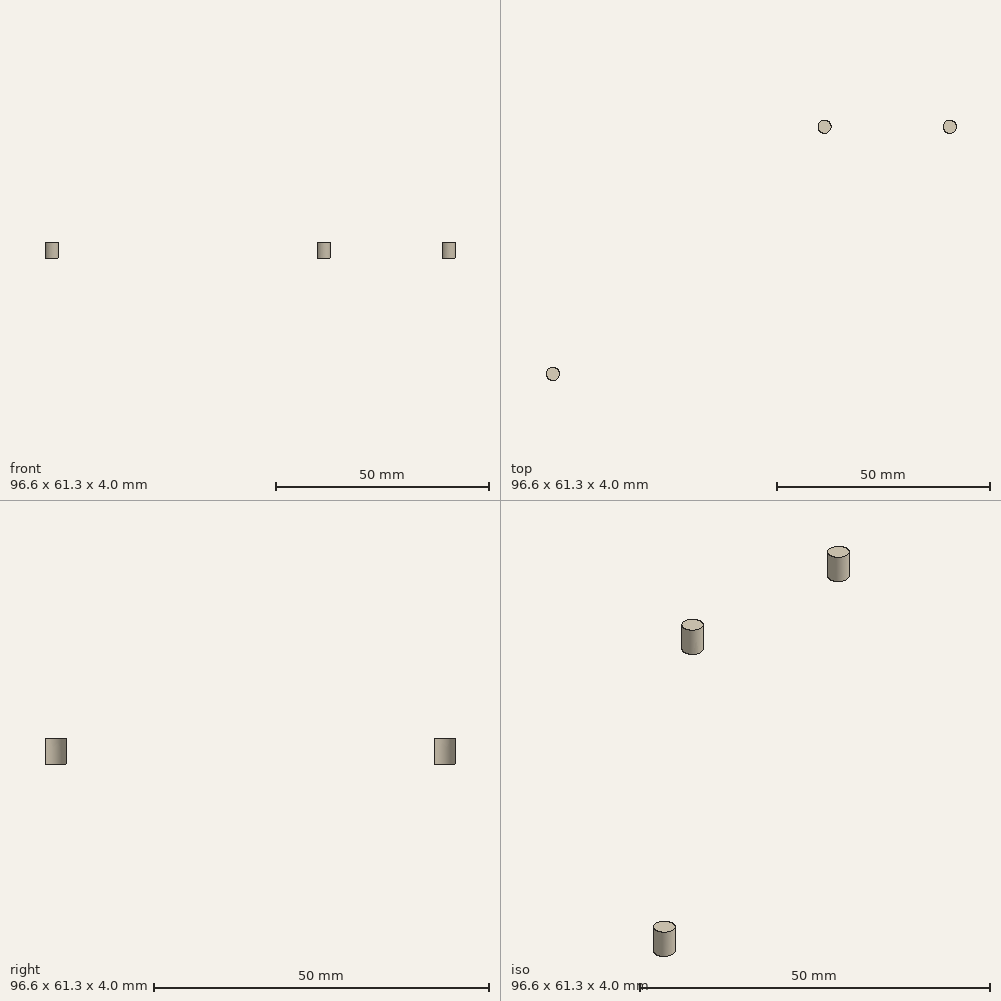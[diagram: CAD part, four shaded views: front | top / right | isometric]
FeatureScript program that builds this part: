
annotation { "Feature Type Name" : "Feature", "Feature Type Description" : "" }
export const myFeature = defineFeature(function(context is Context, id is Id, definition is map)
    precondition{}
    {
        {
            var Q0;
            Q0=qCreatedBy(makeId("Top.planeOp"),FACE);
            var sketch = newSketch(context, id + "F0", { "sketchPlane" : qUnion([Q0])});
            skLineSegment(sketch, "E0.bottom", {"start": v(0, 0) * mm, "end": v(-219, 0) * mm});
            skLineSegment(sketch, "E0.top", {"start": v(0, -219) * mm, "end": v(-219, -219) * mm});
            skLineSegment(sketch, "E0.left", {"start": v(0, 0) * mm, "end": v(0, -219) * mm});
            skLineSegment(sketch, "E0.right", {"start": v(-219, 0) * mm, "end": v(-219, -219) * mm});
            skLineSegment(sketch, "E1", {"start": v(-222.54, -3.54) * mm, "end": v(-219, 0) * mm});
            skLineSegment(sketch, "E2", {"start": v(-219, 0) * mm, "end": v(-215.46, 3.54) * mm});
            skLineSegment(sketch, "E3", {"start": v(-219, 0) * mm, "end": v(0, -219) * mm, "construction": true});
            skLineSegment(sketch, "E4.bottom", {"start": v(-222.54, -3.54) * mm, "end": v(-215.46, 3.54) * mm, "construction": true});
            skLineSegment(sketch, "E4.top", {"start": v(-3.54, -222.54) * mm, "end": v(3.54, -215.46) * mm, "construction": true});
            skLineSegment(sketch, "E4.left", {"start": v(-222.54, -3.54) * mm, "end": v(-3.54, -222.54) * mm, "construction": true});
            skLineSegment(sketch, "E4.right", {"start": v(-215.46, 3.54) * mm, "end": v(3.54, -215.46) * mm, "construction": true});
            skLineSegment(sketch, "E5.bottom", {"start": v(-3.54, 3.54) * mm, "end": v(3.54, -3.54) * mm, "construction": true});
            skLineSegment(sketch, "E5.top", {"start": v(-222.54, -215.46) * mm, "end": v(-215.46, -222.54) * mm, "construction": true});
            skLineSegment(sketch, "E5.left", {"start": v(-3.54, 3.54) * mm, "end": v(-222.54, -215.46) * mm, "construction": true});
            skLineSegment(sketch, "E5.right", {"start": v(3.54, -3.54) * mm, "end": v(-215.46, -222.54) * mm, "construction": true});
            skPoint(sketch, "E6", {"position": v(-215.46, -214.61) * mm});
            skPoint(sketch, "E7", {"position": v(-211.93, -219) * mm});
            skPoint(sketch, "E8", {"position": v(-109.5, -116.57) * mm});
            skPoint(sketch, "E9", {"position": v(-7.07, -219) * mm});
            skLineSegment(sketch, "E10", {"start": v(-211.93, -219) * mm, "end": v(-183.64, -190.72) * mm});
            skLineSegment(sketch, "E11", {"start": v(-183.64, -190.72) * mm, "end": v(-35.36, -190.72) * mm});
            skLineSegment(sketch, "E12", {"start": v(-35.36, -190.72) * mm, "end": v(-7.07, -219) * mm});
            skLineSegment(sketch, "E13", {"start": v(-211.93, -219) * mm, "end": v(-7.07, -219) * mm});
            skPoint(sketch, "E14", {"position": v(-219, -109.5) * mm});
            skPoint(sketch, "E15", {"position": v(0, -109.5) * mm});
            skLineSegment(sketch, "E16", {"start": v(-219, -109.5) * mm, "end": v(0, -109.5) * mm, "construction": true});
            skLineSegment(sketch, "E17.MirrorCS", {"start": v(-211.93, 0) * mm, "end": v(-7.07, 0) * mm});
            skLineSegment(sketch, "E18", {"start": v(-35.36, -28.28) * mm, "end": v(-7.07, 0) * mm});
            skLineSegment(sketch, "E19", {"start": v(-183.64, -28.28) * mm, "end": v(-211.93, 0) * mm});
            skLineSegment(sketch, "E20", {"start": v(-173.04, -180.1) * mm, "end": v(-45.96, -180.1) * mm});
            skLineSegment(sketch, "E21", {"start": v(-45.96, -180.1) * mm, "end": v(-35.36, -190.72) * mm});
            skLineSegment(sketch, "E22", {"start": v(-183.64, -190.72) * mm, "end": v(-173.04, -180.1) * mm});
            skLineSegment(sketch, "E23", {"start": v(-173.04, -180.1) * mm, "end": v(-109.5, -116.57) * mm});
            skLineSegment(sketch, "E24", {"start": v(-45.96, -180.1) * mm, "end": v(-109.5, -116.57) * mm});
            skLineSegment(sketch, "E25", {"start": v(-136.77, -143.84) * mm, "end": v(-82.23, -143.84) * mm});
            skLineSegment(sketch, "E26.MirrorCS", {"start": v(-222.54, -215.46) * mm, "end": v(-219, -219) * mm});
            skLineSegment(sketch, "E27.MirrorCS", {"start": v(-219, -219) * mm, "end": v(-215.46, -222.54) * mm});
            skLineSegment(sketch, "E28.MirrorCS", {"start": v(-183.64, -28.28) * mm, "end": v(-173.04, -38.9) * mm});
            skLineSegment(sketch, "E29.MirrorCS", {"start": v(-45.96, -38.9) * mm, "end": v(-35.36, -28.28) * mm});
            skLineSegment(sketch, "E30.MirrorCS", {"start": v(-45.96, -38.9) * mm, "end": v(-109.5, -102.43) * mm});
            skLineSegment(sketch, "E31.MirrorCS", {"start": v(-183.64, -190.72) * mm, "end": v(-211.93, -219) * mm});
            skLineSegment(sketch, "E32.MirrorCS", {"start": v(3.54, -215.46) * mm, "end": v(-215.46, 3.54) * mm, "construction": true});
            skLineSegment(sketch, "E33.MirrorCS", {"start": v(-183.64, -28.28) * mm, "end": v(-35.36, -28.28) * mm});
            skLineSegment(sketch, "E34.MirrorCS", {"start": v(-136.77, -75.16) * mm, "end": v(-82.23, -75.16) * mm});
            skLineSegment(sketch, "E35.MirrorCS", {"start": v(-219, -219) * mm, "end": v(0, 0) * mm, "construction": true});
            skPoint(sketch, "E36.MirrorP", {"position": v(-211.93, 0) * mm});
            skPoint(sketch, "E37.MirrorP", {"position": v(-7.07, 0) * mm});
            skLineSegment(sketch, "E38.MirrorCS", {"start": v(-173.04, -38.9) * mm, "end": v(-109.5, -102.43) * mm});
            skPoint(sketch, "E39.MirrorP", {"position": v(-109.5, -102.43) * mm});
            skPoint(sketch, "E40.MirrorP", {"position": v(-215.46, -4.39) * mm});
            skLineSegment(sketch, "E41.MirrorCS", {"start": v(-219, -219) * mm, "end": v(-219, 0) * mm});
            skLineSegment(sketch, "E42.MirrorCS", {"start": v(-3.54, -222.54) * mm, "end": v(-222.54, -3.54) * mm, "construction": true});
            skLineSegment(sketch, "E43.MirrorCS", {"start": v(-211.93, 0) * mm, "end": v(-183.64, -28.28) * mm});
            skLineSegment(sketch, "E44.MirrorCS", {"start": v(-222.54, -215.46) * mm, "end": v(-3.54, 3.54) * mm, "construction": true});
            skLineSegment(sketch, "E45.MirrorCS", {"start": v(-215.46, -222.54) * mm, "end": v(3.54, -3.54) * mm, "construction": true});
            skLineSegment(sketch, "E46.MirrorCS", {"start": v(-173.04, -38.9) * mm, "end": v(-45.96, -38.9) * mm});
            skLineSegment(sketch, "E47.MirrorCS", {"start": v(0, -219) * mm, "end": v(0, 0) * mm});
            skLineSegment(sketch, "E48", {"start": v(-219, -7.07) * mm, "end": v(-194.25, -31.82) * mm});
            skLineSegment(sketch, "E49", {"start": v(-190.72, -183.64) * mm, "end": v(-219, -211.93) * mm});
            skLineSegment(sketch, "E50", {"start": v(-219, -211.93) * mm, "end": v(-219, -7.07) * mm});
            skLineSegment(sketch, "E51", {"start": v(-194.25, -31.82) * mm, "end": v(-194.25, -71.82) * mm});
            skLineSegment(sketch, "E52", {"start": v(-194.25, -71.82) * mm, "end": v(-219, -96.57) * mm});
            skLineSegment(sketch, "E53.MirrorCS", {"start": v(-194.25, -147.18) * mm, "end": v(-219, -122.43) * mm});
            skLineSegment(sketch, "E54.MirrorCS", {"start": v(-194.25, -187.18) * mm, "end": v(-194.25, -147.18) * mm});
            skLineSegment(sketch, "E55", {"start": v(-194.25, -187.18) * mm, "end": v(-219, -211.93) * mm});
            skLineSegment(sketch, "E56", {"start": v(-219, -122.43) * mm, "end": v(-219, -211.93) * mm});
            skLineSegment(sketch, "E57", {"start": v(-219, -96.57) * mm, "end": v(-219, -7.07) * mm});
            skLineSegment(sketch, "E58", {"start": v(-109.5, -219) * mm, "end": v(-109.5, 0) * mm, "construction": true});
            skLineSegment(sketch, "E59", {"start": v(0, -96.57) * mm, "end": v(0, -122.43) * mm, "construction": true});
            skPoint(sketch, "E60", {"position": v(-24.75, -109.5) * mm});
            skLineSegment(sketch, "E61", {"start": v(0, -65) * mm, "end": v(0, -147.18) * mm});
            skLineSegment(sketch, "E62", {"start": v(0, -7.07) * mm, "end": v(-17.68, -24.75) * mm});
            skLineSegment(sketch, "E63", {"start": v(0, -65) * mm, "end": v(-17.68, -47.32) * mm});
            skLineSegment(sketch, "E64", {"start": v(-17.68, -47.32) * mm, "end": v(-17.68, -24.75) * mm});
            skLineSegment(sketch, "E65.MirrorCS", {"start": v(0, -154) * mm, "end": v(-17.68, -171.68) * mm});
            skLineSegment(sketch, "E66.MirrorCS", {"start": v(-17.68, -171.68) * mm, "end": v(-17.68, -194.25) * mm});
            skLineSegment(sketch, "E67", {"start": v(-17.68, -194.25) * mm, "end": v(0, -211.93) * mm});
            skLineSegment(sketch, "E68", {"start": v(0, -211.93) * mm, "end": v(0, -154) * mm});
            skPoint(sketch, "E69", {"position": v(0, -142) * mm});
            skPoint(sketch, "E70", {"position": v(0, -77) * mm});
            skLineSegment(sketch, "E71", {"start": v(-17.68, -122.43) * mm, "end": v(-17.68, -96.57) * mm});
            skLineSegment(sketch, "E72", {"start": v(-17.68, -122.43) * mm, "end": v(0, -142) * mm});
            skLineSegment(sketch, "E73", {"start": v(-17.68, -96.57) * mm, "end": v(0, -77) * mm});
            skLineSegment(sketch, "E74", {"start": v(-17.68, -122.43) * mm, "end": v(0, -122.43) * mm, "construction": true});
            skLineSegment(sketch, "E75", {"start": v(0, -96.57) * mm, "end": v(-17.68, -96.57) * mm, "construction": true});
            skLineSegment(sketch, "E76", {"start": v(-214, -91.57) * mm, "end": v(-214, -127.43) * mm});
            skLineSegment(sketch, "E77", {"start": v(-10, -55) * mm, "end": v(-10, -88.07) * mm});
            skLineSegment(sketch, "E78.MirrorCS", {"start": v(-10, -164) * mm, "end": v(-10, -130.93) * mm});
            skLineSegment(sketch, "E79.bottom", {"start": v(-145.72, -81.22) * mm, "end": v(-117.43, -109.5) * mm});
            skLineSegment(sketch, "E79.top", {"start": v(-174, -109.5) * mm, "end": v(-145.72, -137.78) * mm});
            skLineSegment(sketch, "E79.left", {"start": v(-145.72, -81.22) * mm, "end": v(-174, -109.5) * mm});
            skLineSegment(sketch, "E79.right", {"start": v(-117.43, -109.5) * mm, "end": v(-145.72, -137.78) * mm});
            skLineSegment(sketch, "E80", {"start": v(-174, -109.5) * mm, "end": v(-219, -109.5) * mm, "construction": true});
            skLineSegment(sketch, "E81", {"start": v(-149.25, -84.75) * mm, "end": v(-142.18, -84.75) * mm});
            skLineSegment(sketch, "E82.MirrorCS", {"start": v(-149.25, -134.25) * mm, "end": v(-142.18, -134.25) * mm});
            skLineSegment(sketch, "E83", {"start": v(-170.46, -105.96) * mm, "end": v(-170.46, -113.04) * mm});
            skLineSegment(sketch, "E84", {"start": v(-145.72, -81.22) * mm, "end": v(-145.72, -137.78) * mm, "construction": true});
            skLineSegment(sketch, "E85.MirrorCS", {"start": v(-120.97, -105.96) * mm, "end": v(-120.97, -113.04) * mm});
            skLineSegment(sketch, "E86.MirrorCS", {"start": v(-73.28, -81.22) * mm, "end": v(-45, -109.5) * mm});
            skLineSegment(sketch, "E87.MirrorCS", {"start": v(-73.28, -81.22) * mm, "end": v(-101.57, -109.5) * mm});
            skLineSegment(sketch, "E88.MirrorCS", {"start": v(-101.57, -109.5) * mm, "end": v(-73.28, -137.78) * mm});
            skLineSegment(sketch, "E89.MirrorCS", {"start": v(-45, -109.5) * mm, "end": v(-73.28, -137.78) * mm});
            skLineSegment(sketch, "E90.MirrorCS", {"start": v(-48.54, -105.96) * mm, "end": v(-48.54, -113.04) * mm});
            skLineSegment(sketch, "E91.MirrorCS", {"start": v(-69.75, -84.75) * mm, "end": v(-76.82, -84.75) * mm});
            skLineSegment(sketch, "E92.MirrorCS", {"start": v(-98.03, -105.96) * mm, "end": v(-98.03, -113.04) * mm});
            skLineSegment(sketch, "E93.MirrorCS", {"start": v(-69.75, -134.25) * mm, "end": v(-76.82, -134.25) * mm});
            skPoint(sketch, "E94", {"position": v(-5, -5) * mm});
            skCircle(sketch, "E95", {"center": v(-5, -5) * mm, "radius": 1.52 * mm});
            skCircle(sketch, "E96.MirrorC", {"center": v(-214, -5) * mm, "radius": 1.52 * mm});
            skCircle(sketch, "E97.MirrorC", {"center": v(-214, -214) * mm, "radius": 1.52 * mm});
            skCircle(sketch, "E98.MirrorC", {"center": v(-5, -214) * mm, "radius": 1.52 * mm});
            skSolve(sketch);
        }
        {
            var Q0;
            {var subQ19=sQuery(id+"F0.wireOp",EDGE,"E28.MirrorCS");Q0=makeQuery(id+"F0.imprint","IMPRINT",FACE,{"disambiguationData":[TD([[makeQuery(id+"F0.imprint","IMPRINT",EDGE,{"derivedFrom":subQ19}),-1.0]])]});}
            var Q1;
            Q1=makeQuery(id+"F0.imprint","IMPRINT",FACE,{"disambiguationData":[TD([[makeQuery(id+"F0.imprint","IMPRINT",EDGE,{"derivedFrom":sQuery(id+"F0.wireOp",EDGE,"E21")}),-1.0]])]});
            var Q2;
            {var subQ3=sQuery(id+"F0.wireOp",EDGE,"E25");Q2=makeQuery(id+"F0.imprint","IMPRINT",FACE,{"disambiguationData":[TD([[makeQuery(id+"F0.imprint","IMPRINT",EDGE,{"derivedFrom":subQ3}),1.0]])]});}
            var Q3;
            {var subQ3=sQuery(id+"F0.wireOp",EDGE,"E34.MirrorCS");Q3=makeQuery(id+"F0.imprint","IMPRINT",FACE,{"disambiguationData":[TD([[makeQuery(id+"F0.imprint","IMPRINT",EDGE,{"derivedFrom":subQ3}),-1.0]])]});}
            var Q4;
            Q4=makeQuery(id+"F0.imprint","IMPRINT",FACE,{"disambiguationData":[TD([[makeQuery(id+"F0.imprint","IMPRINT",EDGE,{"derivedFrom":sQuery(id+"F0.wireOp",EDGE,"E28.MirrorCS")}),1.0]])]});
            var Q5;
            {var subQ3=sQuery(id+"F0.wireOp",EDGE,"E81");Q5=makeQuery(id+"F0.imprint","IMPRINT",FACE,{"disambiguationData":[TD([[makeQuery(id+"F0.imprint","IMPRINT",EDGE,{"derivedFrom":subQ3}),1.0]])]});}
            var Q6;
            {var subQ3=sQuery(id+"F0.wireOp",EDGE,"E83");Q6=makeQuery(id+"F0.imprint","IMPRINT",FACE,{"disambiguationData":[TD([[makeQuery(id+"F0.imprint","IMPRINT",EDGE,{"derivedFrom":subQ3}),-1.0]])]});}
            var Q7;
            {var subQ3=sQuery(id+"F0.wireOp",EDGE,"E82.MirrorCS");Q7=makeQuery(id+"F0.imprint","IMPRINT",FACE,{"disambiguationData":[TD([[makeQuery(id+"F0.imprint","IMPRINT",EDGE,{"derivedFrom":subQ3}),-1.0]])]});}
            var Q8;
            {var subQ3=sQuery(id+"F0.wireOp",EDGE,"E85.MirrorCS");Q8=makeQuery(id+"F0.imprint","IMPRINT",FACE,{"disambiguationData":[TD([[makeQuery(id+"F0.imprint","IMPRINT",EDGE,{"derivedFrom":subQ3}),1.0]])]});}
            var Q9;
            {var subQ3=sQuery(id+"F0.wireOp",EDGE,"E91.MirrorCS");Q9=makeQuery(id+"F0.imprint","IMPRINT",FACE,{"disambiguationData":[TD([[makeQuery(id+"F0.imprint","IMPRINT",EDGE,{"derivedFrom":subQ3}),-1.0]])]});}
            var Q10;
            {var subQ3=sQuery(id+"F0.wireOp",EDGE,"E92.MirrorCS");Q10=makeQuery(id+"F0.imprint","IMPRINT",FACE,{"disambiguationData":[TD([[makeQuery(id+"F0.imprint","IMPRINT",EDGE,{"derivedFrom":subQ3}),-1.0]])]});}
            var Q11;
            {var subQ3=sQuery(id+"F0.wireOp",EDGE,"E93.MirrorCS");Q11=makeQuery(id+"F0.imprint","IMPRINT",FACE,{"disambiguationData":[TD([[makeQuery(id+"F0.imprint","IMPRINT",EDGE,{"derivedFrom":subQ3}),1.0]])]});}
            var Q12;
            {var subQ3=sQuery(id+"F0.wireOp",EDGE,"E90.MirrorCS");Q12=makeQuery(id+"F0.imprint","IMPRINT",FACE,{"disambiguationData":[TD([[makeQuery(id+"F0.imprint","IMPRINT",EDGE,{"derivedFrom":subQ3}),1.0]])]});}
            extrude(context, id + "F1", {"entities" : qUnion([Q0, Q1, Q2, Q3, Q4, Q5, Q6, Q7, Q8, Q9, Q10, Q11, Q12]), "depth" : 4 * mm, "offsetDistance" : 25 * mm});
        }
        {
            var Q0;
            Q0=makeQuery(id+"F1.opExtrude","SWEPT_EDGE",EDGE,{"disambiguationData":[OSD([sQuery(id+"F0.wireOp",EDGE,"E79.left"),sQuery(id+"F0.wireOp",EDGE,"E81")])]});
            var Q1;
            Q1=makeQuery(id+"F1.opExtrude","SWEPT_EDGE",EDGE,{"disambiguationData":[OSD([sQuery(id+"F0.wireOp",EDGE,"E79.bottom"),sQuery(id+"F0.wireOp",EDGE,"E81")])]});
            var Q2;
            Q2=makeQuery(id+"F1.opExtrude","SWEPT_EDGE",EDGE,{"disambiguationData":[OSD([sQuery(id+"F0.wireOp",EDGE,"E79.left"),sQuery(id+"F0.wireOp",EDGE,"E83")])]});
            var Q3;
            Q3=makeQuery(id+"F1.opExtrude","SWEPT_EDGE",EDGE,{"disambiguationData":[OSD([sQuery(id+"F0.wireOp",EDGE,"E79.top"),sQuery(id+"F0.wireOp",EDGE,"E83")])]});
            var Q4;
            Q4=makeQuery(id+"F1.opExtrude","SWEPT_EDGE",EDGE,{"disambiguationData":[OSD([sQuery(id+"F0.wireOp",EDGE,"E79.right"),sQuery(id+"F0.wireOp",EDGE,"E85.MirrorCS")])]});
            var Q5;
            Q5=makeQuery(id+"F1.opExtrude","SWEPT_EDGE",EDGE,{"disambiguationData":[OSD([sQuery(id+"F0.wireOp",EDGE,"E79.bottom"),sQuery(id+"F0.wireOp",EDGE,"E85.MirrorCS")])]});
            var Q6;
            Q6=makeQuery(id+"F1.opExtrude","SWEPT_EDGE",EDGE,{"disambiguationData":[OSD([sQuery(id+"F0.wireOp",EDGE,"E79.right"),sQuery(id+"F0.wireOp",EDGE,"E82.MirrorCS")])]});
            var Q7;
            Q7=makeQuery(id+"F1.opExtrude","SWEPT_EDGE",EDGE,{"disambiguationData":[OSD([sQuery(id+"F0.wireOp",EDGE,"E79.top"),sQuery(id+"F0.wireOp",EDGE,"E82.MirrorCS")])]});
            var Q8;
            Q8=makeQuery(id+"F1.opExtrude","SWEPT_EDGE",EDGE,{"disambiguationData":[OSD([sQuery(id+"F0.wireOp",EDGE,"E87.MirrorCS"),sQuery(id+"F0.wireOp",EDGE,"E91.MirrorCS")])]});
            var Q9;
            Q9=makeQuery(id+"F1.opExtrude","SWEPT_EDGE",EDGE,{"disambiguationData":[OSD([sQuery(id+"F0.wireOp",EDGE,"E86.MirrorCS"),sQuery(id+"F0.wireOp",EDGE,"E91.MirrorCS")])]});
            var Q10;
            Q10=makeQuery(id+"F1.opExtrude","SWEPT_EDGE",EDGE,{"disambiguationData":[OSD([sQuery(id+"F0.wireOp",EDGE,"E87.MirrorCS"),sQuery(id+"F0.wireOp",EDGE,"E92.MirrorCS")])]});
            var Q11;
            Q11=makeQuery(id+"F1.opExtrude","SWEPT_EDGE",EDGE,{"disambiguationData":[OSD([sQuery(id+"F0.wireOp",EDGE,"E88.MirrorCS"),sQuery(id+"F0.wireOp",EDGE,"E92.MirrorCS")])]});
            var Q12;
            Q12=makeQuery(id+"F1.opExtrude","SWEPT_EDGE",EDGE,{"disambiguationData":[OSD([sQuery(id+"F0.wireOp",EDGE,"E86.MirrorCS"),sQuery(id+"F0.wireOp",EDGE,"E90.MirrorCS")])]});
            var Q13;
            Q13=makeQuery(id+"F1.opExtrude","SWEPT_EDGE",EDGE,{"disambiguationData":[OSD([sQuery(id+"F0.wireOp",EDGE,"E89.MirrorCS"),sQuery(id+"F0.wireOp",EDGE,"E90.MirrorCS")])]});
            var Q14;
            Q14=makeQuery(id+"F1.opExtrude","SWEPT_EDGE",EDGE,{"disambiguationData":[OSD([sQuery(id+"F0.wireOp",EDGE,"E89.MirrorCS"),sQuery(id+"F0.wireOp",EDGE,"E93.MirrorCS")])]});
            var Q15;
            Q15=makeQuery(id+"F1.opExtrude","SWEPT_EDGE",EDGE,{"disambiguationData":[OSD([sQuery(id+"F0.wireOp",EDGE,"E88.MirrorCS"),sQuery(id+"F0.wireOp",EDGE,"E93.MirrorCS")])]});
            var Q16;
            Q16=makeQuery(id+"F1.opExtrude","SWEPT_EDGE",EDGE,{"disambiguationData":[OSD([sQuery(id+"F0.wireOp",EDGE,"E23"),sQuery(id+"F0.wireOp",EDGE,"E25")])]});
            var Q17;
            Q17=makeQuery(id+"F1.opExtrude","SWEPT_EDGE",EDGE,{"disambiguationData":[OSD([sQuery(id+"F0.wireOp",EDGE,"E24"),sQuery(id+"F0.wireOp",EDGE,"E25")])]});
            var Q18;
            Q18=makeQuery(id+"F1.opExtrude","SWEPT_EDGE",EDGE,{"disambiguationData":[OSD([sQuery(id+"F0.wireOp",EDGE,"E30.MirrorCS"),sQuery(id+"F0.wireOp",EDGE,"E34.MirrorCS")])]});
            var Q19;
            Q19=makeQuery(id+"F1.opExtrude","SWEPT_EDGE",EDGE,{"disambiguationData":[OSD([sQuery(id+"F0.wireOp",EDGE,"E38.MirrorCS"),sQuery(id+"F0.wireOp",EDGE,"E34.MirrorCS")])]});
            var Q20;
            Q20=makeQuery(id+"F1.opExtrude","SWEPT_EDGE",EDGE,{"disambiguationData":[OSD([sQuery(id+"F0.wireOp",EDGE,"E21"),sQuery(id+"F0.wireOp",EDGE,"E12"),sQuery(id+"F0.wireOp",EDGE,"E11")])]});
            var Q21;
            Q21=makeQuery(id+"F1.opExtrude","SWEPT_EDGE",EDGE,{"disambiguationData":[OSD([sQuery(id+"F0.wireOp",EDGE,"E22"),sQuery(id+"F0.wireOp",EDGE,"E31.MirrorCS"),sQuery(id+"F0.wireOp",EDGE,"E11")])]});
            var Q22;
            Q22=makeQuery(id+"F1.opExtrude","SWEPT_EDGE",EDGE,{"disambiguationData":[OSD([sQuery(id+"F0.wireOp",EDGE,"E28.MirrorCS"),sQuery(id+"F0.wireOp",EDGE,"E19"),sQuery(id+"F0.wireOp",EDGE,"E33.MirrorCS")])]});
            var Q23;
            Q23=makeQuery(id+"F1.opExtrude","SWEPT_EDGE",EDGE,{"disambiguationData":[OSD([sQuery(id+"F0.wireOp",EDGE,"E29.MirrorCS"),sQuery(id+"F0.wireOp",EDGE,"E18"),sQuery(id+"F0.wireOp",EDGE,"E33.MirrorCS")])]});
            var Q24;
            Q24=makeQuery(id+"F1.opExtrude","SWEPT_EDGE",EDGE,{"disambiguationData":[OSD([sQuery(id+"F0.wireOp",EDGE,"E62"),sQuery(id+"F0.wireOp",EDGE,"E64")])]});
            var Q25;
            Q25=makeQuery(id+"F1.opExtrude","SWEPT_EDGE",EDGE,{"disambiguationData":[OSD([sQuery(id+"F0.wireOp",EDGE,"E63"),sQuery(id+"F0.wireOp",EDGE,"E64")])]});
            var Q26;
            Q26=makeQuery(id+"F1.opExtrude","SWEPT_EDGE",EDGE,{"disambiguationData":[OSD([sQuery(id+"F0.wireOp",EDGE,"E63"),sQuery(id+"F0.wireOp",EDGE,"E77")])]});
            var Q27;
            Q27=makeQuery(id+"F1.opExtrude","SWEPT_EDGE",EDGE,{"disambiguationData":[OSD([sQuery(id+"F0.wireOp",EDGE,"E73"),sQuery(id+"F0.wireOp",EDGE,"E77")])]});
            var Q28;
            Q28=makeQuery(id+"F1.opExtrude","SWEPT_EDGE",EDGE,{"disambiguationData":[OSD([sQuery(id+"F0.wireOp",EDGE,"E71"),sQuery(id+"F0.wireOp",EDGE,"E73")])]});
            var Q29;
            Q29=makeQuery(id+"F1.opExtrude","SWEPT_EDGE",EDGE,{"disambiguationData":[OSD([sQuery(id+"F0.wireOp",EDGE,"E71"),sQuery(id+"F0.wireOp",EDGE,"E72")])]});
            var Q30;
            Q30=makeQuery(id+"F1.opExtrude","SWEPT_EDGE",EDGE,{"disambiguationData":[OSD([sQuery(id+"F0.wireOp",EDGE,"E72"),sQuery(id+"F0.wireOp",EDGE,"E78.MirrorCS")])]});
            var Q31;
            Q31=makeQuery(id+"F1.opExtrude","SWEPT_EDGE",EDGE,{"disambiguationData":[OSD([sQuery(id+"F0.wireOp",EDGE,"E65.MirrorCS"),sQuery(id+"F0.wireOp",EDGE,"E78.MirrorCS")])]});
            var Q32;
            Q32=makeQuery(id+"F1.opExtrude","SWEPT_EDGE",EDGE,{"disambiguationData":[OSD([sQuery(id+"F0.wireOp",EDGE,"E65.MirrorCS"),sQuery(id+"F0.wireOp",EDGE,"E66.MirrorCS")])]});
            var Q33;
            Q33=makeQuery(id+"F1.opExtrude","SWEPT_EDGE",EDGE,{"disambiguationData":[OSD([sQuery(id+"F0.wireOp",EDGE,"E66.MirrorCS"),sQuery(id+"F0.wireOp",EDGE,"E67")])]});
            var Q34;
            Q34=makeQuery(id+"F1.opExtrude","SWEPT_EDGE",EDGE,{"disambiguationData":[OSD([sQuery(id+"F0.wireOp",EDGE,"E51"),sQuery(id+"F0.wireOp",EDGE,"E52")])]});
            var Q35;
            Q35=makeQuery(id+"F1.opExtrude","SWEPT_EDGE",EDGE,{"disambiguationData":[OSD([sQuery(id+"F0.wireOp",EDGE,"E48"),sQuery(id+"F0.wireOp",EDGE,"E51")])]});
            var Q36;
            Q36=makeQuery(id+"F1.opExtrude","SWEPT_EDGE",EDGE,{"disambiguationData":[OSD([sQuery(id+"F0.wireOp",EDGE,"E52"),sQuery(id+"F0.wireOp",EDGE,"E76")])]});
            var Q37;
            Q37=makeQuery(id+"F1.opExtrude","SWEPT_EDGE",EDGE,{"disambiguationData":[OSD([sQuery(id+"F0.wireOp",EDGE,"E53.MirrorCS"),sQuery(id+"F0.wireOp",EDGE,"E76")])]});
            var Q38;
            Q38=makeQuery(id+"F1.opExtrude","SWEPT_EDGE",EDGE,{"disambiguationData":[OSD([sQuery(id+"F0.wireOp",EDGE,"E53.MirrorCS"),sQuery(id+"F0.wireOp",EDGE,"E54.MirrorCS")])]});
            var Q39;
            Q39=makeQuery(id+"F1.opExtrude","SWEPT_EDGE",EDGE,{"disambiguationData":[OSD([sQuery(id+"F0.wireOp",EDGE,"E54.MirrorCS"),sQuery(id+"F0.wireOp",EDGE,"E55")])]});
            fillet(context, id + "F2", {"entities" : qUnion([Q0, Q1, Q2, Q3, Q4, Q5, Q6, Q7, Q8, Q9, Q10, Q11, Q12, Q13, Q14, Q15, Q16, Q17, Q18, Q19, Q20, Q21, Q22, Q23, Q24, Q25, Q26, Q27, Q28, Q29, Q30, Q31, Q32, Q33, Q34, Q35, Q36, Q37, Q38, Q39]), "radius" : 5 * mm, "tangentPropagation" : true, "allowEdgeOverflow" : false});
        }
        {
            var Q0;
            Q0=makeQuery(id+"F1.opExtrude","SWEPT_EDGE",EDGE,{"disambiguationData":[OSD([sQuery(id+"F0.wireOp",EDGE,"E21"),sQuery(id+"F0.wireOp",EDGE,"E24"),sQuery(id+"F0.wireOp",EDGE,"E20")])]});
            var Q1;
            Q1=makeQuery(id+"F1.opExtrude","SWEPT_EDGE",EDGE,{"disambiguationData":[OSD([sQuery(id+"F0.wireOp",EDGE,"E22"),sQuery(id+"F0.wireOp",EDGE,"E23"),sQuery(id+"F0.wireOp",EDGE,"E20")])]});
            var Q2;
            Q2=makeQuery(id+"F1.opExtrude","SWEPT_EDGE",EDGE,{"disambiguationData":[OSD([sQuery(id+"F0.wireOp",EDGE,"E28.MirrorCS"),sQuery(id+"F0.wireOp",EDGE,"E38.MirrorCS"),sQuery(id+"F0.wireOp",EDGE,"E46.MirrorCS")])]});
            var Q3;
            Q3=makeQuery(id+"F1.opExtrude","SWEPT_EDGE",EDGE,{"disambiguationData":[OSD([sQuery(id+"F0.wireOp",EDGE,"E29.MirrorCS"),sQuery(id+"F0.wireOp",EDGE,"E30.MirrorCS"),sQuery(id+"F0.wireOp",EDGE,"E46.MirrorCS")])]});
            fillet(context, id + "F3", {"entities" : qUnion([Q0, Q1, Q2, Q3]), "radius" : 3 * mm, "tangentPropagation" : true, "allowEdgeOverflow" : false});
        }
        {
            var Q0;
            Q0=makeQuery(id+"F1.opExtrude","SWEPT_EDGE",EDGE,{"disambiguationData":[OSD([sQuery(id+"F0.wireOp",EDGE,"E0.bottom"),sQuery(id+"F0.wireOp",EDGE,"E0.right")])]});
            var Q1;
            Q1=makeQuery(id+"F1.opExtrude","SWEPT_EDGE",EDGE,{"disambiguationData":[OSD([sQuery(id+"F0.wireOp",EDGE,"E0.right"),sQuery(id+"F0.wireOp",EDGE,"E48"),sQuery(id+"F0.wireOp",EDGE,"E57")])]});
            var Q2;
            Q2=makeQuery(id+"F1.opExtrude","SWEPT_EDGE",EDGE,{"disambiguationData":[OSD([sQuery(id+"F0.wireOp",EDGE,"E19"),sQuery(id+"F0.wireOp",EDGE,"E0.bottom"),sQuery(id+"F0.wireOp",EDGE,"E17.MirrorCS")])]});
            var Q3;
            Q3=makeQuery(id+"F1.opExtrude","SWEPT_EDGE",EDGE,{"disambiguationData":[OSD([sQuery(id+"F0.wireOp",EDGE,"E18"),sQuery(id+"F0.wireOp",EDGE,"E0.bottom"),sQuery(id+"F0.wireOp",EDGE,"E17.MirrorCS")])]});
            var Q4;
            Q4=makeQuery(id+"F1.opExtrude","SWEPT_EDGE",EDGE,{"disambiguationData":[OSD([sQuery(id+"F0.wireOp",EDGE,"E0.bottom"),sQuery(id+"F0.wireOp",EDGE,"E0.left")])]});
            var Q5;
            Q5=makeQuery(id+"F1.opExtrude","SWEPT_EDGE",EDGE,{"disambiguationData":[OSD([sQuery(id+"F0.wireOp",EDGE,"E0.left"),sQuery(id+"F0.wireOp",EDGE,"E62")])]});
            var Q6;
            Q6=makeQuery(id+"F1.opExtrude","SWEPT_EDGE",EDGE,{"disambiguationData":[OSD([sQuery(id+"F0.wireOp",EDGE,"E0.top"),sQuery(id+"F0.wireOp",EDGE,"E0.left")])]});
            var Q7;
            Q7=makeQuery(id+"F1.opExtrude","SWEPT_EDGE",EDGE,{"disambiguationData":[OSD([sQuery(id+"F0.wireOp",EDGE,"E0.top"),sQuery(id+"F0.wireOp",EDGE,"E12"),sQuery(id+"F0.wireOp",EDGE,"E13")])]});
            var Q8;
            Q8=makeQuery(id+"F1.opExtrude","SWEPT_EDGE",EDGE,{"disambiguationData":[OSD([sQuery(id+"F0.wireOp",EDGE,"E31.MirrorCS"),sQuery(id+"F0.wireOp",EDGE,"E0.top"),sQuery(id+"F0.wireOp",EDGE,"E13")])]});
            var Q9;
            Q9=makeQuery(id+"F1.opExtrude","SWEPT_EDGE",EDGE,{"disambiguationData":[OSD([sQuery(id+"F0.wireOp",EDGE,"E0.top"),sQuery(id+"F0.wireOp",EDGE,"E0.right")])]});
            var Q10;
            Q10=makeQuery(id+"F1.opExtrude","SWEPT_EDGE",EDGE,{"disambiguationData":[OSD([sQuery(id+"F0.wireOp",EDGE,"E0.right"),sQuery(id+"F0.wireOp",EDGE,"E55"),sQuery(id+"F0.wireOp",EDGE,"E56")])]});
            var Q11;
            Q11=makeQuery(id+"F1.opExtrude","SWEPT_EDGE",EDGE,{"disambiguationData":[OSD([sQuery(id+"F0.wireOp",EDGE,"E0.left"),sQuery(id+"F0.wireOp",EDGE,"E67"),sQuery(id+"F0.wireOp",EDGE,"E68")])]});
            fillet(context, id + "F4", {"entities" : qUnion([Q0, Q1, Q2, Q3, Q4, Q5, Q6, Q7, Q8, Q9, Q10, Q11]), "radius" : 4.75 * mm, "tangentPropagation" : true, "allowEdgeOverflow" : false});
        }
        {
            var Q0;
            Q0=makeQuery(id+"F1.opExtrude","CAP_FACE",FACE,{"disambiguationData":[OSD([sQuery(id+"F0.wireOp",EDGE,"E30.MirrorCS"),sQuery(id+"F0.wireOp",EDGE,"E23"),sQuery(id+"F0.wireOp",EDGE,"E31.MirrorCS"),sQuery(id+"F0.wireOp",EDGE,"E0.top"),sQuery(id+"F0.wireOp",EDGE,"E24"),sQuery(id+"F0.wireOp",EDGE,"E38.MirrorCS"),sQuery(id+"F0.wireOp",EDGE,"E19"),sQuery(id+"F0.wireOp",EDGE,"E18"),sQuery(id+"F0.wireOp",EDGE,"E12"),sQuery(id+"F0.wireOp",EDGE,"E0.bottom"),sQuery(id+"F0.wireOp",EDGE,"E34.MirrorCS"),sQuery(id+"F0.wireOp",EDGE,"E33.MirrorCS"),sQuery(id+"F0.wireOp",EDGE,"E25"),sQuery(id+"F0.wireOp",EDGE,"E20"),sQuery(id+"F0.wireOp",EDGE,"E0.left"),sQuery(id+"F0.wireOp",EDGE,"E0.right"),sQuery(id+"F0.wireOp",EDGE,"E11"),sQuery(id+"F0.wireOp",EDGE,"E46.MirrorCS"),sQuery(id+"F0.wireOp",EDGE,"E48"),sQuery(id+"F0.wireOp",EDGE,"E51"),sQuery(id+"F0.wireOp",EDGE,"E52"),sQuery(id+"F0.wireOp",EDGE,"E53.MirrorCS"),sQuery(id+"F0.wireOp",EDGE,"E54.MirrorCS"),sQuery(id+"F0.wireOp",EDGE,"E55"),sQuery(id+"F0.wireOp",EDGE,"E62"),sQuery(id+"F0.wireOp",EDGE,"E63"),sQuery(id+"F0.wireOp",EDGE,"E64"),sQuery(id+"F0.wireOp",EDGE,"E65.MirrorCS"),sQuery(id+"F0.wireOp",EDGE,"E66.MirrorCS"),sQuery(id+"F0.wireOp",EDGE,"E67"),sQuery(id+"F0.wireOp",EDGE,"E71"),sQuery(id+"F0.wireOp",EDGE,"E72"),sQuery(id+"F0.wireOp",EDGE,"E73"),sQuery(id+"F0.wireOp",EDGE,"E76"),sQuery(id+"F0.wireOp",EDGE,"E77"),sQuery(id+"F0.wireOp",EDGE,"E78.MirrorCS"),sQuery(id+"F0.wireOp",EDGE,"E79.bottom"),sQuery(id+"F0.wireOp",EDGE,"E79.top"),sQuery(id+"F0.wireOp",EDGE,"E79.left"),sQuery(id+"F0.wireOp",EDGE,"E79.right"),sQuery(id+"F0.wireOp",EDGE,"E81"),sQuery(id+"F0.wireOp",EDGE,"E82.MirrorCS"),sQuery(id+"F0.wireOp",EDGE,"E83"),sQuery(id+"F0.wireOp",EDGE,"E85.MirrorCS"),sQuery(id+"F0.wireOp",EDGE,"E86.MirrorCS"),sQuery(id+"F0.wireOp",EDGE,"E87.MirrorCS"),sQuery(id+"F0.wireOp",EDGE,"E88.MirrorCS"),sQuery(id+"F0.wireOp",EDGE,"E89.MirrorCS"),sQuery(id+"F0.wireOp",EDGE,"E90.MirrorCS"),sQuery(id+"F0.wireOp",EDGE,"E91.MirrorCS"),sQuery(id+"F0.wireOp",EDGE,"E92.MirrorCS"),sQuery(id+"F0.wireOp",EDGE,"E93.MirrorCS"),sQuery(id+"F0.wireOp",EDGE,"E95"),sQuery(id+"F0.wireOp",EDGE,"E96.MirrorC"),sQuery(id+"F0.wireOp",EDGE,"E97.MirrorC"),sQuery(id+"F0.wireOp",EDGE,"E98.MirrorC")])],"isStart":true});
            var sketch = newSketch(context, id + "F5", { "sketchPlane" : qUnion([Q0])});
            skPoint(sketch, "E99", {"position": v(-108.97, 89.16) * mm});
            skCircle(sketch, "E100", {"center": v(-108.97, 89.16) * mm, "radius": 1.55 * mm});
            skLineSegment(sketch, "E101", {"start": v(-17.68, 109.5) * mm, "end": v(-214, 109.5) * mm, "construction": true});
            skCircle(sketch, "E102.MirrorC", {"center": v(-108.97, 129.84) * mm, "radius": 1.55 * mm});
            skPoint(sketch, "E103", {"position": v(-15.5, 147.4) * mm});
            skPoint(sketch, "E103.positionSnap0", {"position": v(-10, 147.4) * mm});
            skPoint(sketch, "E104", {"position": v(-45, 147.4) * mm});
            skCircle(sketch, "E105", {"center": v(-15.5, 147.4) * mm, "radius": 1.55 * mm});
            skCircle(sketch, "E106", {"center": v(-45, 147.4) * mm, "radius": 1.55 * mm});
            skPoint(sketch, "E107.MirrorP", {"position": v(-15.5, 71.6) * mm});
            skPoint(sketch, "E108.MirrorP", {"position": v(-45, 71.6) * mm});
            skCircle(sketch, "E109.MirrorC", {"center": v(-15.5, 71.6) * mm, "radius": 1.55 * mm});
            skCircle(sketch, "E110.MirrorC", {"center": v(-45, 71.6) * mm, "radius": 1.55 * mm});
            skPoint(sketch, "E111", {"position": v(-208.5, 109.5) * mm});
            skPoint(sketch, "E112", {"position": v(-179, 109.5) * mm});
            skCircle(sketch, "E113", {"center": v(-208.5, 109.5) * mm, "radius": 1.55 * mm});
            skCircle(sketch, "E114", {"center": v(-179, 109.5) * mm, "radius": 1.55 * mm});
            skSolve(sketch);
        }
        {
            var Q0;
            Q0=makeQuery(id+"F5.imprint","IMPRINT",FACE,{"disambiguationData":[TD([[makeQuery(id+"F5.imprint","IMPRINT",EDGE,{"derivedFrom":sQuery(id+"F5.wireOp",EDGE,"E102.MirrorC")}),-1.0]])]});
            var Q1;
            Q1=makeQuery(id+"F5.imprint","IMPRINT",FACE,{"disambiguationData":[TD([[makeQuery(id+"F5.imprint","IMPRINT",EDGE,{"derivedFrom":sQuery(id+"F5.wireOp",EDGE,"E100")}),1.0]])]});
            var Q2;
            Q2=makeQuery(id+"F5.imprint","IMPRINT",FACE,{"disambiguationData":[TD([[makeQuery(id+"F5.imprint","IMPRINT",EDGE,{"derivedFrom":sQuery(id+"F5.wireOp",EDGE,"E106")}),1.0]])]});
            var Q3;
            Q3=makeQuery(id+"F5.imprint","IMPRINT",FACE,{"disambiguationData":[TD([[makeQuery(id+"F5.imprint","IMPRINT",EDGE,{"derivedFrom":sQuery(id+"F5.wireOp",EDGE,"E105")}),1.0]])]});
            var Q4;
            Q4=makeQuery(id+"F5.imprint","IMPRINT",FACE,{"disambiguationData":[TD([[makeQuery(id+"F5.imprint","IMPRINT",EDGE,{"derivedFrom":sQuery(id+"F5.wireOp",EDGE,"E110.MirrorC")}),-1.0]])]});
            var Q5;
            Q5=makeQuery(id+"F5.imprint","IMPRINT",FACE,{"disambiguationData":[TD([[makeQuery(id+"F5.imprint","IMPRINT",EDGE,{"derivedFrom":sQuery(id+"F5.wireOp",EDGE,"E109.MirrorC")}),-1.0]])]});
            var Q6;
            Q6=makeQuery(id+"F5.imprint","IMPRINT",FACE,{"disambiguationData":[TD([[makeQuery(id+"F5.imprint","IMPRINT",EDGE,{"derivedFrom":sQuery(id+"F5.wireOp",EDGE,"E114")}),1.0]])]});
            var Q7;
            Q7=makeQuery(id+"F5.imprint","IMPRINT",FACE,{"disambiguationData":[TD([[makeQuery(id+"F5.imprint","IMPRINT",EDGE,{"derivedFrom":sQuery(id+"F5.wireOp",EDGE,"E113")}),1.0]])]});
            extrude(context, id + "F6", {"entities" : qUnion([Q0, Q1, Q2, Q3, Q4, Q5, Q6, Q7]), "operationType" : NewBodyOperationType.REMOVE, "endBound" : BoundingType.THROUGH_ALL, "oppositeDirection" : true, "depth" : 25 * mm, "offsetDistance" : 25 * mm});
        }
    });
